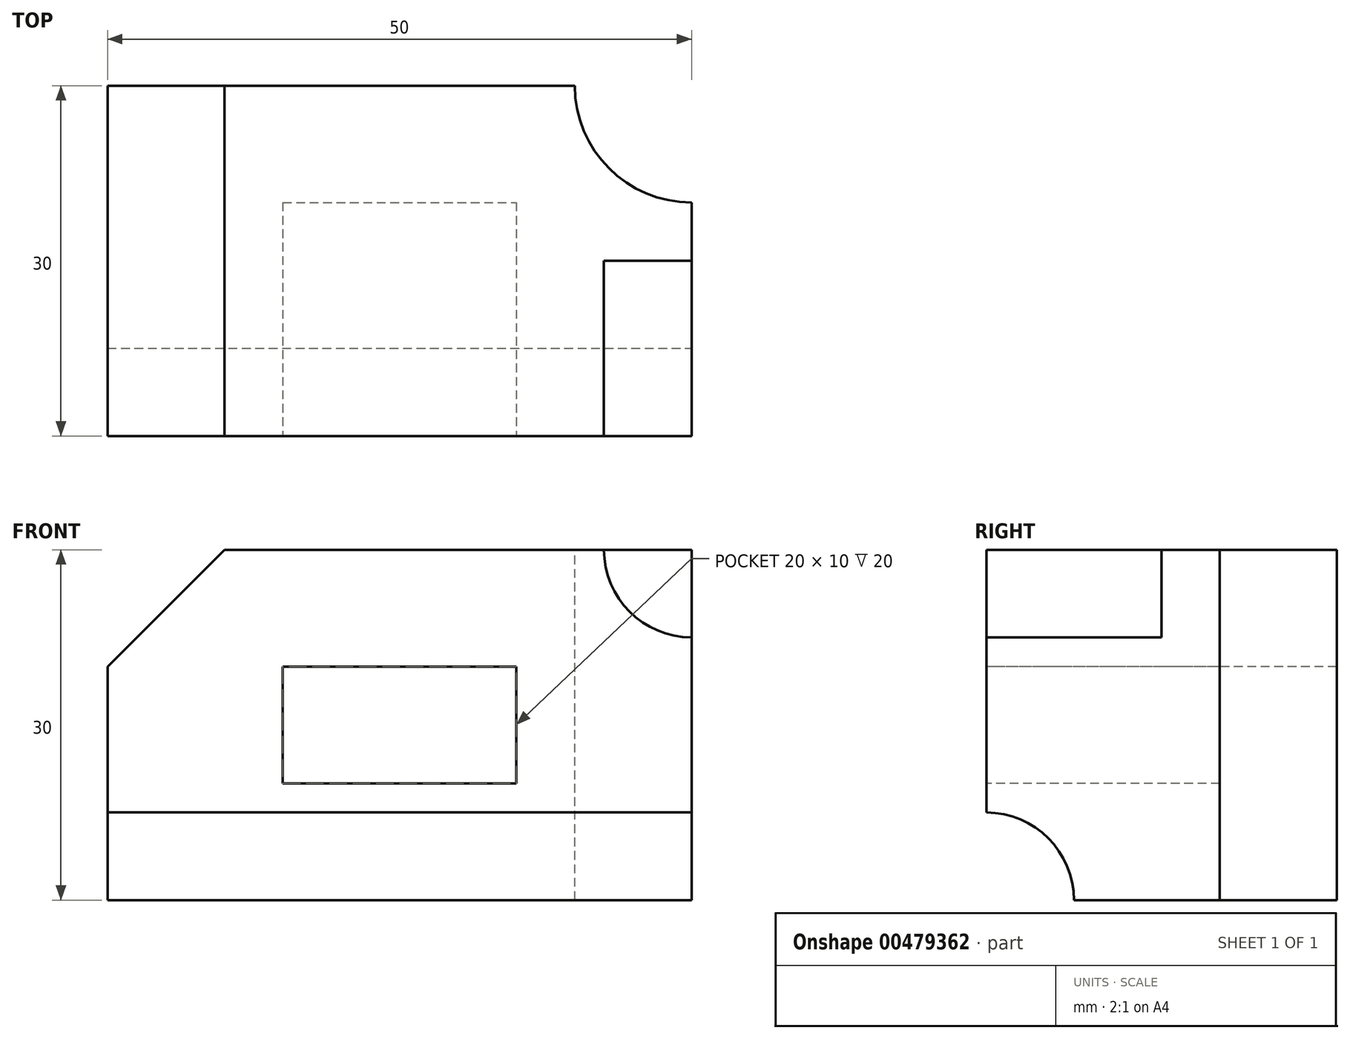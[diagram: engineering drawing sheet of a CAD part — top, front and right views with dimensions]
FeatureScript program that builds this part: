
annotation { "Feature Type Name" : "Feature", "Feature Type Description" : "" }
export const myFeature = defineFeature(function(context is Context, id is Id, definition is map)
    precondition{}
    {
        {
            var Q0;
            Q0=qCreatedBy(makeId("Top.planeOp"),FACE);
            var sketch = newSketch(context, id + "F0", { "sketchPlane" : qUnion([Q0])});
            skLineSegment(sketch, "E0.bottom", {"start": v(0, 0) * mm, "end": v(50, 0) * mm});
            skLineSegment(sketch, "E0.top", {"start": v(0, 30) * mm, "end": v(50, 30) * mm});
            skLineSegment(sketch, "E0.left", {"start": v(0, 0) * mm, "end": v(0, 30) * mm});
            skLineSegment(sketch, "E0.right", {"start": v(50, 0) * mm, "end": v(50, 30) * mm});
            skSolve(sketch);
        }
        {
            var Q0;
            Q0 = qSketchRegion(id + "F0", true);
            extrude(context, id + "F1", {"entities" : qUnion([Q0]), "depth" : 30 * mm});
        }
        {
            var Q0;
            Q0=makeQuery(id+"F1.opExtrude","CAP_FACE",FACE,{"disambiguationData":[OSD([sQuery(id+"F0.wireOp",EDGE,"E0.bottom"),sQuery(id+"F0.wireOp",EDGE,"E0.top"),sQuery(id+"F0.wireOp",EDGE,"E0.left"),sQuery(id+"F0.wireOp",EDGE,"E0.right")])],"isStart":false});
            var sketch = newSketch(context, id + "F2", { "sketchPlane" : qUnion([Q0])});
            skCircle(sketch, "E1", {"center": v(50, 30) * mm, "radius": 10 * mm});
            skSolve(sketch);
        }
        {
            var Q0;
            Q0 = qSketchRegion(id + "F2", true);
            extrude(context, id + "F3", {"entities" : qUnion([Q0]), "operationType" : NewBodyOperationType.REMOVE, "endBound" : BoundingType.THROUGH_ALL, "oppositeDirection" : true, "depth" : 25 * mm});
        }
        {
            var Q0;
            Q0=makeQuery(id+"F1.opExtrude","SWEPT_FACE",FACE,{"disambiguationData":[OSD([sQuery(id+"F0.wireOp",EDGE,"E0.bottom")])]});
            var sketch = newSketch(context, id + "F4", { "sketchPlane" : qUnion([Q0])});
            skLineSegment(sketch, "E2", {"start": v(10, 30) * mm, "end": v(0, 20) * mm});
            skSolve(sketch);
        }
        {
            var Q0;
            Q0 = qSketchRegion(id + "F4", true);
            var Q1;
            {var subQ0=sQuery(id+"F4.wireOp",EDGE,"E2");Q1=makeQuery(id+"F4.imprint","IMPRINT",FACE,{"disambiguationData":[TD([[makeQuery(id+"F4.imprint","IMPRINT",EDGE,{"derivedFrom":subQ0}),-1.0]])]});}
            extrude(context, id + "F5", {"entities" : qUnion([Q0, Q1]), "operationType" : NewBodyOperationType.REMOVE, "endBound" : BoundingType.THROUGH_ALL, "oppositeDirection" : true, "depth" : 25 * mm});
        }
        {
            var Q0;
            Q0=makeQuery(id+"F1.opExtrude","SWEPT_FACE",FACE,{"disambiguationData":[OSD([sQuery(id+"F0.wireOp",EDGE,"E0.bottom")])]});
            var sketch = newSketch(context, id + "F6", { "sketchPlane" : qUnion([Q0])});
            skLineSegment(sketch, "E3.bottom", {"start": v(15, 20) * mm, "end": v(35, 20) * mm});
            skLineSegment(sketch, "E3.top", {"start": v(15, 10) * mm, "end": v(35, 10) * mm});
            skLineSegment(sketch, "E3.left", {"start": v(15, 20) * mm, "end": v(15, 10) * mm});
            skLineSegment(sketch, "E3.right", {"start": v(35, 20) * mm, "end": v(35, 10) * mm});
            skSolve(sketch);
        }
        {
            var Q0;
            Q0 = qSketchRegion(id + "F6", true);
            extrude(context, id + "F7", {"entities" : qUnion([Q0]), "operationType" : NewBodyOperationType.REMOVE, "oppositeDirection" : true, "depth" : 20 * mm});
        }
        {
            var Q0;
            Q0=makeQuery(id+"F1.opExtrude","SWEPT_FACE",FACE,{"disambiguationData":[OSD([sQuery(id+"F0.wireOp",EDGE,"E0.right")])]});
            var sketch = newSketch(context, id + "F8", { "sketchPlane" : qUnion([Q0])});
            skCircle(sketch, "E4", {"center": v(0, 0) * mm, "radius": 7.5 * mm});
            skSolve(sketch);
        }
        {
            var Q0;
            Q0 = qSketchRegion(id + "F8", true);
            extrude(context, id + "F9", {"entities" : qUnion([Q0]), "operationType" : NewBodyOperationType.REMOVE, "endBound" : BoundingType.THROUGH_ALL, "oppositeDirection" : true, "depth" : 25 * mm});
        }
        {
            var Q0;
            Q0=makeQuery(id+"F1.opExtrude","SWEPT_FACE",FACE,{"disambiguationData":[OSD([sQuery(id+"F0.wireOp",EDGE,"E0.bottom")])]});
            var sketch = newSketch(context, id + "F10", { "sketchPlane" : qUnion([Q0])});
            skCircle(sketch, "E5", {"center": v(50, 30) * mm, "radius": 7.5 * mm});
            skSolve(sketch);
        }
        {
            var Q0;
            Q0 = qSketchRegion(id + "F10", true);
            extrude(context, id + "F11", {"entities" : qUnion([Q0]), "operationType" : NewBodyOperationType.REMOVE, "oppositeDirection" : true, "depth" : 15 * mm});
        }
    });
